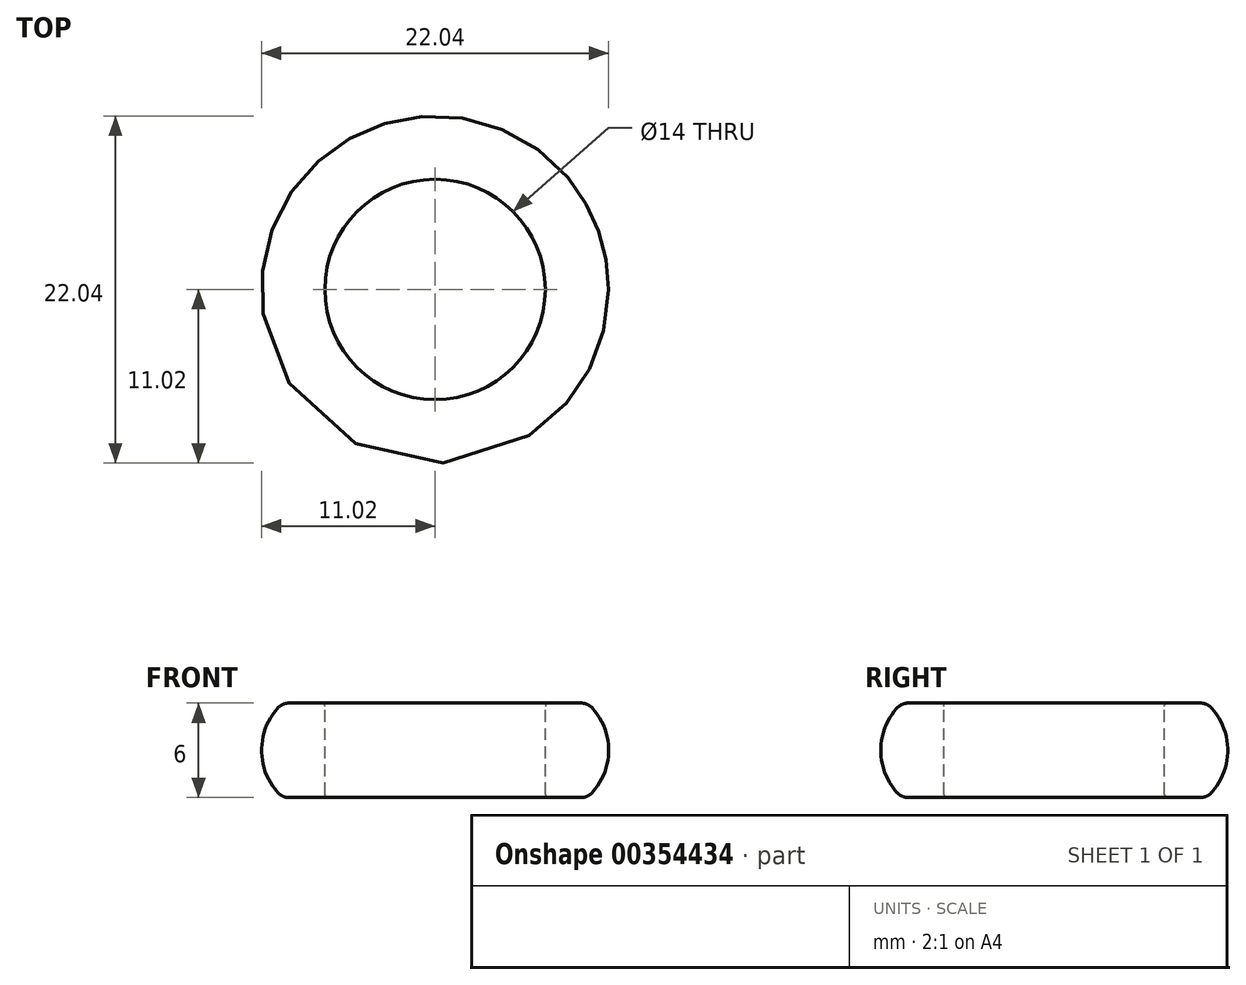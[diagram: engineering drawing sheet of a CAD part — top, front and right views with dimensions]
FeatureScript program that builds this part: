
annotation { "Feature Type Name" : "Feature", "Feature Type Description" : "" }
export const myFeature = defineFeature(function(context is Context, id is Id, definition is map)
    precondition{}
    {
        {
            var Q0;
            Q0=qCreatedBy(makeId("Front.planeOp"),FACE);
            var sketch = newSketch(context, id + "F0", { "sketchPlane" : qUnion([Q0])});
            skLineSegment(sketch, "E0", {"start": v(-7, 0.2) * mm, "end": v(-7, 5.8) * mm});
            skLineSegment(sketch, "E1", {"start": v(-7.2, 6) * mm, "end": v(-9.26, 6) * mm});
            skLineSegment(sketch, "E2", {"start": v(-7.2, 0) * mm, "end": v(-9.26, 0) * mm});
            skArc(sketch, "E3", {"start": v(-10.01, 0.34) * mm, "mid": v(-11.02, 3) * mm, "end": v(-10.01, 5.66) * mm});
            skPoint(sketch, "E4.visualSharp", {"position": v(-9.68, 6) * mm});
            skArc(sketch, "E4.filletArc", {"start": v(-9.26, 6) * mm, "mid": v(-9.67, 5.91) * mm, "end": v(-10.01, 5.66) * mm});
            skPoint(sketch, "E5.visualSharp", {"position": v(-9.68, 0) * mm});
            skArc(sketch, "E5.filletArc", {"start": v(-10.01, 0.34) * mm, "mid": v(-9.67, 0.09) * mm, "end": v(-9.26, 0) * mm});
            skPoint(sketch, "E6.visualSharp", {"position": v(-7, 6) * mm});
            skArc(sketch, "E6.filletArc", {"start": v(-7, 5.8) * mm, "mid": v(-7.06, 5.94) * mm, "end": v(-7.2, 6) * mm});
            skPoint(sketch, "E7.visualSharp", {"position": v(-7, 0) * mm});
            skArc(sketch, "E7.filletArc", {"start": v(-7.2, 0) * mm, "mid": v(-7.06, 0.06) * mm, "end": v(-7, 0.2) * mm});
            skLineSegment(sketch, "E8", {"start": v(0, 10) * mm, "end": v(0, 0) * mm});
            skSolve(sketch);
        }
        {
            var Q0;
            Q0=makeQuery(id+"F0.imprint","IMPRINT",FACE,{"disambiguationData":[TD([[makeQuery(id+"F0.imprint","IMPRINT",EDGE,{"derivedFrom":sQuery(id+"F0.wireOp",EDGE,"E0")}),1.0]])]});
            var Q1;
            Q1=sQuery(id+"F0.wireOp",EDGE,"E8");
            revolve(context, id + "F1", {"entities" : qUnion([Q0]), "axis" : qUnion([Q1]), "revolveType" : RevolveType.FULL});
        }
    });
